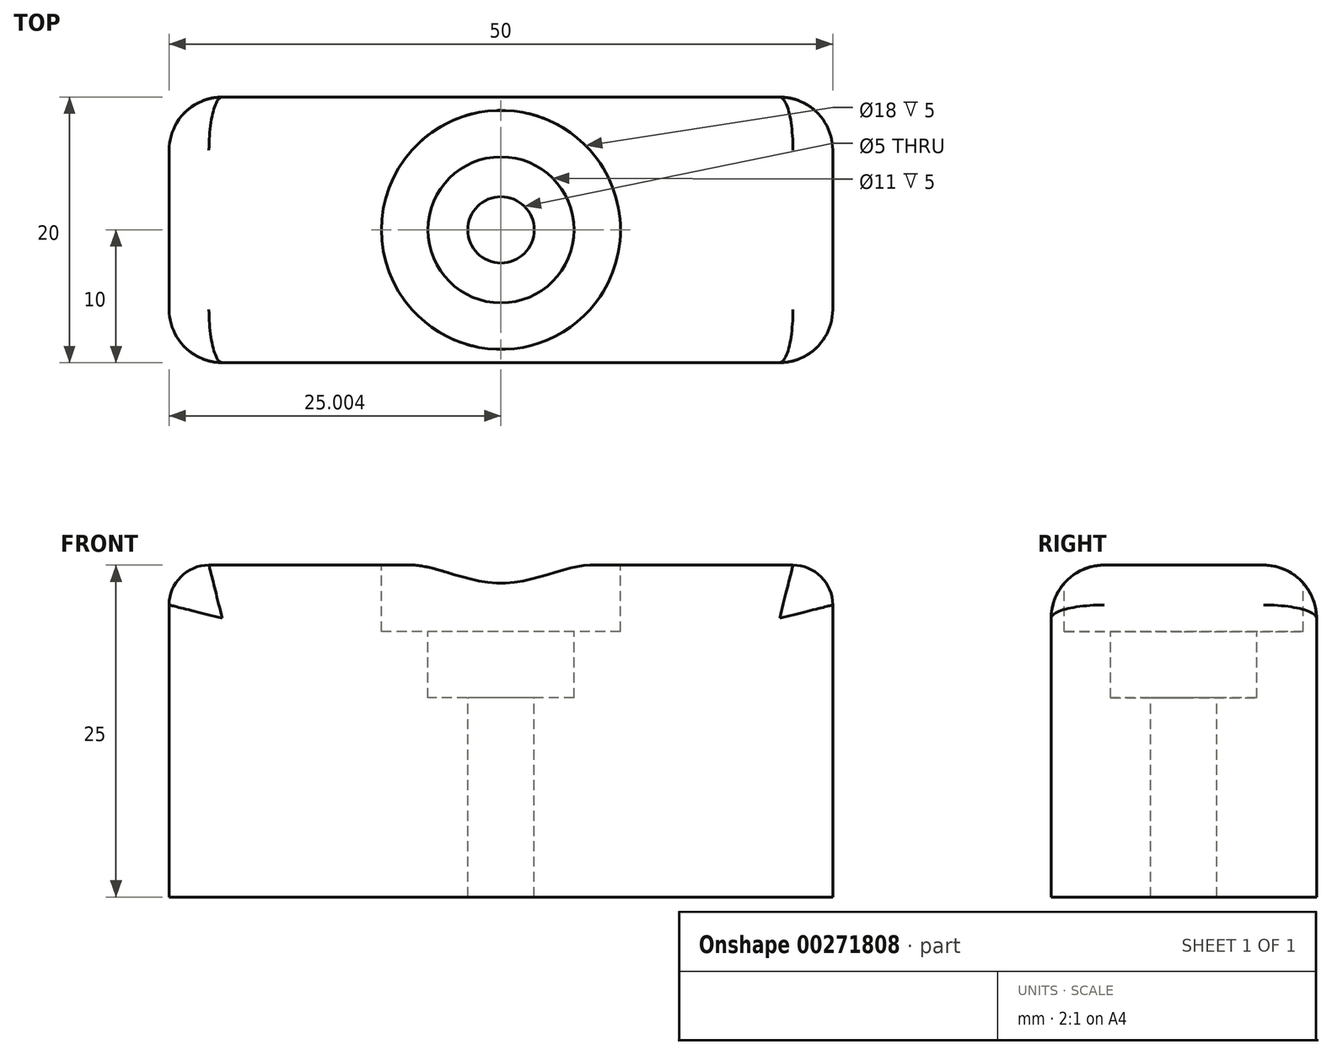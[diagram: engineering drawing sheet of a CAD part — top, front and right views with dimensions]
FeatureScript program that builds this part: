
annotation { "Feature Type Name" : "Feature", "Feature Type Description" : "" }
export const myFeature = defineFeature(function(context is Context, id is Id, definition is map)
    precondition{}
    {
        {
            var Q0;
            Q0=qCreatedBy(makeId("Top.planeOp"),FACE);
            var sketch = newSketch(context, id + "F0", { "sketchPlane" : qUnion([Q0])});
            skLineSegment(sketch, "E0.bottom", {"start": v(18.74, 16.83) * mm, "end": v(-31.26, 16.83) * mm});
            skLineSegment(sketch, "E0.top", {"start": v(18.74, -3.17) * mm, "end": v(-31.26, -3.17) * mm});
            skLineSegment(sketch, "E0.left", {"start": v(18.74, 16.83) * mm, "end": v(18.74, -3.17) * mm});
            skLineSegment(sketch, "E0.right", {"start": v(-31.26, 16.83) * mm, "end": v(-31.26, -3.17) * mm});
            skSolve(sketch);
        }
        {
            var Q0;
            Q0=qSketchRegion(id+"F0",true);
            extrude(context, id + "F1", {"entities" : qUnion([Q0]), "depth" : 25 * mm});
        }
        {
            var Q0;
            Q0=makeQuery(id+"F1.opExtrude","CAP_FACE",FACE,{"disambiguationData":[OSD([sQuery(id+"F0.wireOp",EDGE,"E0.bottom"),sQuery(id+"F0.wireOp",EDGE,"E0.top"),sQuery(id+"F0.wireOp",EDGE,"E0.left"),sQuery(id+"F0.wireOp",EDGE,"E0.right")])],"isStart":false});
            var sketch = newSketch(context, id + "F2", { "sketchPlane" : qUnion([Q0])});
            skCircle(sketch, "E1", {"center": v(-6.26, 6.83) * mm, "radius": 9 * mm});
            skPoint(sketch, "E1.centerSnap0", {"position": v(-6.26, 16.83) * mm});
            skPoint(sketch, "E1.centerSnap1", {"position": v(-31.26, 6.83) * mm});
            skSolve(sketch);
        }
        {
            var Q0;
            Q0=qSketchRegion(id+"F2",true);
            extrude(context, id + "F3", {"entities" : qUnion([Q0]), "operationType" : NewBodyOperationType.REMOVE, "oppositeDirection" : true, "depth" : 5 * mm});
        }
        {
            var Q0;
            Q0=makeQuery(id+"F3.boolean.opBoolean","COPY",FACE,{"derivedFrom":makeQuery(id+"F3.opExtrude","CAP_FACE",FACE,{"disambiguationData":[OSD([sQuery(id+"F2.wireOp",EDGE,"E1")])],"isStart":false})});
            var sketch = newSketch(context, id + "F4", { "sketchPlane" : qUnion([Q0])});
            skPoint(sketch, "E2", {"position": v(-6.26, 6.83) * mm});
            skSolve(sketch);
        }
        {
            var Q0;
            Q0=sQuery(id+"F4.wireOp",VERTEX,"E2");
            var Q1;
            Q1=makeQuery(id+"F1.opExtrude","SWEPT_BODY",BODY,{"disambiguationData":[OSD([sQuery(id+"F0.wireOp",EDGE,"E0.bottom"),sQuery(id+"F0.wireOp",EDGE,"E0.top"),sQuery(id+"F0.wireOp",EDGE,"E0.left"),sQuery(id+"F0.wireOp",EDGE,"E0.right")])]});
            hole(context, id + "F5", {"style" : HoleStyle.C_BORE, "endStyle" : HoleEndStyle.THROUGH, "holeDiameter" : 5 * mm, "cBoreDiameter" : 11 * mm, "cBoreDepth" : 5 * mm, "startFromSketch" : true, "locations" : qUnion([Q0]), "scope" : qUnion([Q1]), "isTappedThrough" : true});
        }
        {
            var Q0;
            Q0=makeQuery(id+"F1.opExtrude","SWEPT_EDGE",EDGE,{"disambiguationData":[OSD([sQuery(id+"F0.wireOp",EDGE,"E0.bottom"),sQuery(id+"F0.wireOp",EDGE,"E0.right")])]});
            var Q1;
            Q1=makeQuery(id+"F1.opExtrude","SWEPT_EDGE",EDGE,{"disambiguationData":[OSD([sQuery(id+"F0.wireOp",EDGE,"E0.bottom"),sQuery(id+"F0.wireOp",EDGE,"E0.left")])]});
            var Q2;
            Q2=makeQuery(id+"F1.opExtrude","SWEPT_EDGE",EDGE,{"disambiguationData":[OSD([sQuery(id+"F0.wireOp",EDGE,"E0.top"),sQuery(id+"F0.wireOp",EDGE,"E0.left")])]});
            var Q3;
            Q3=makeQuery(id+"F1.opExtrude","SWEPT_EDGE",EDGE,{"disambiguationData":[OSD([sQuery(id+"F0.wireOp",EDGE,"E0.top"),sQuery(id+"F0.wireOp",EDGE,"E0.right")])]});
            var Q4;
            Q4=makeQuery(id+"F1.opExtrude","CAP_EDGE",EDGE,{"disambiguationData":[OSD([sQuery(id+"F0.wireOp",EDGE,"E0.top")])],"isStart":false});
            var Q5;
            Q5=makeQuery(id+"F1.opExtrude","CAP_EDGE",EDGE,{"disambiguationData":[OSD([sQuery(id+"F0.wireOp",EDGE,"E0.bottom")])],"isStart":false});
            fillet(context, id + "F6", {"entities" : qUnion([Q0, Q1, Q2, Q3, Q4, Q5]), "radius" : 4 * mm, "tangentPropagation" : true, "allowEdgeOverflow" : false});
        }
        {
            var Q0;
            Q0=makeQuery(id+"F1.opExtrude","CAP_EDGE",EDGE,{"disambiguationData":[OSD([sQuery(id+"F0.wireOp",EDGE,"E0.left")])],"isStart":false});
            var Q1;
            Q1=makeQuery(id+"F1.opExtrude","CAP_EDGE",EDGE,{"disambiguationData":[OSD([sQuery(id+"F0.wireOp",EDGE,"E0.right")])],"isStart":false});
            fillet(context, id + "F7", {"entities" : qUnion([Q0, Q1]), "radius" : 3 * mm, "tangentPropagation" : true, "allowEdgeOverflow" : false});
        }
    });
